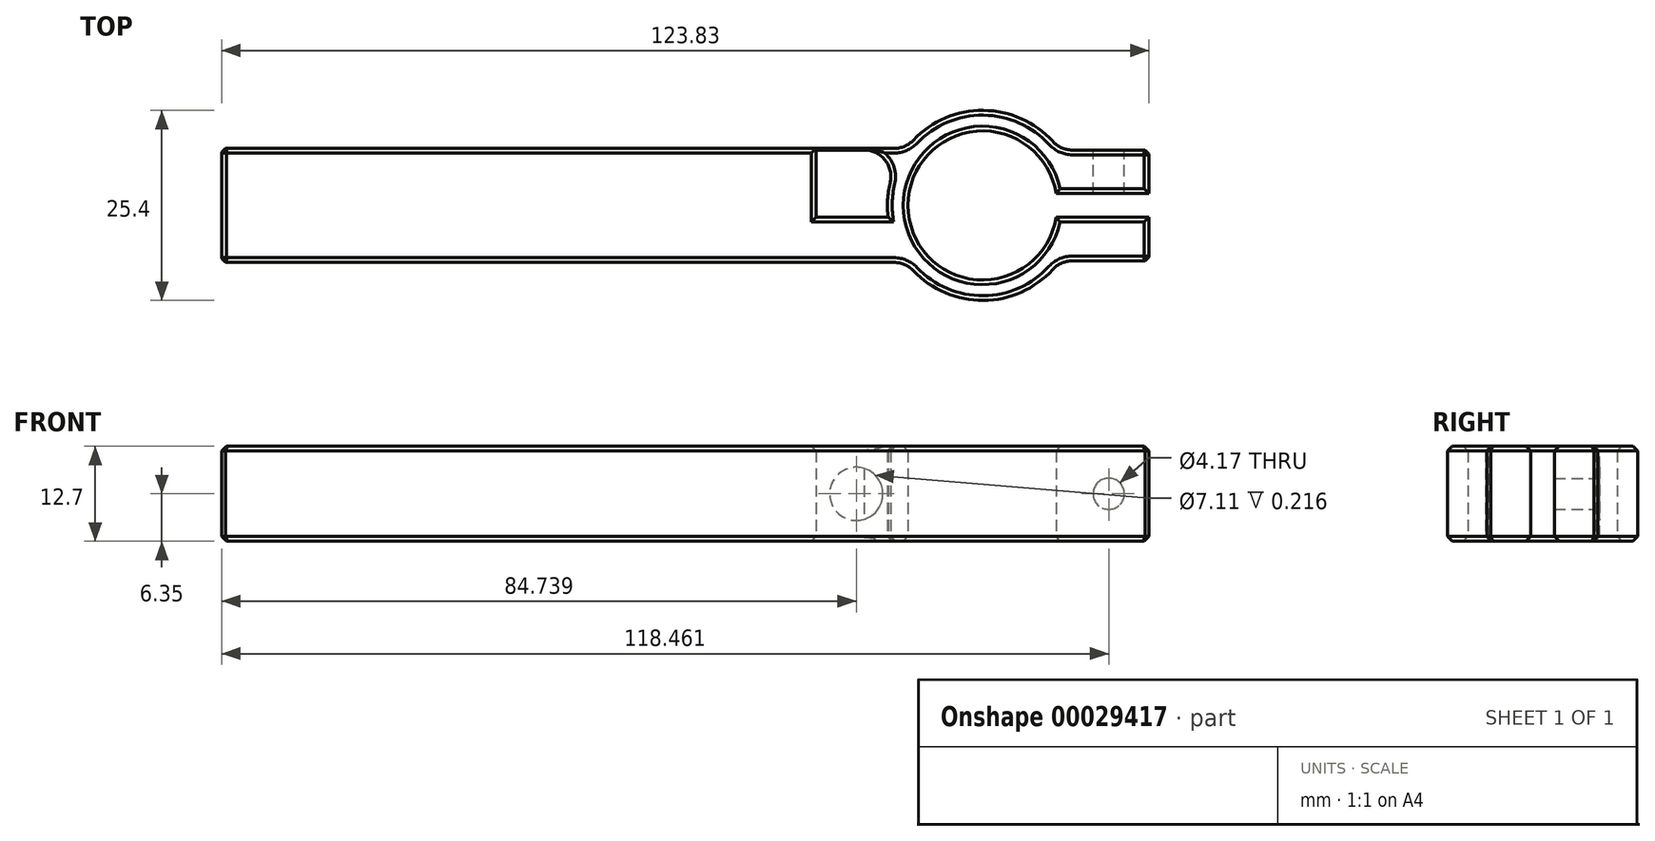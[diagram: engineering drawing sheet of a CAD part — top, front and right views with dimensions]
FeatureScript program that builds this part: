
annotation { "Feature Type Name" : "Feature", "Feature Type Description" : "" }
export const myFeature = defineFeature(function(context is Context, id is Id, definition is map)
    precondition{}
    {
        {
            var Q0;
            Q0=qCreatedBy(makeId("Top.planeOp"),FACE);
            var sketch = newSketch(context, id + "F0", { "sketchPlane" : qUnion([Q0])});
            skCircle(sketch, "E0", {"center": v(0, 0) * mm, "radius": 9.96 * mm});
            skCircle(sketch, "E1", {"center": v(0, 0) * mm, "radius": 12.7 * mm});
            skPoint(sketch, "E2.rect.middle", {"position": v(-50.8, 0) * mm});
            skLineSegment(sketch, "E3.rect.bottom", {"start": v(0, 7.62) * mm, "end": v(-101.6, 7.62) * mm});
            skLineSegment(sketch, "E3.rect.top", {"start": v(0, -7.62) * mm, "end": v(-101.6, -7.62) * mm});
            skLineSegment(sketch, "E3.rect.left", {"start": v(0, 7.62) * mm, "end": v(0, -7.62) * mm});
            skLineSegment(sketch, "E3.rect.right", {"start": v(-101.6, 7.62) * mm, "end": v(-101.6, -7.62) * mm});
            skLineSegment(sketch, "E4", {"start": v(-12.19, 0) * mm, "end": v(-50.8, 0) * mm, "construction": true});
            skLineSegment(sketch, "E5.rect.bottom", {"start": v(33.33, 1.59) * mm, "end": v(-33.33, 1.59) * mm});
            skLineSegment(sketch, "E5.rect.top", {"start": v(33.33, -1.59) * mm, "end": v(-33.33, -1.59) * mm});
            skLineSegment(sketch, "E5.rect.left", {"start": v(33.33, 1.59) * mm, "end": v(33.33, -1.59) * mm});
            skLineSegment(sketch, "E5.rect.right", {"start": v(-33.33, 1.59) * mm, "end": v(-33.33, -1.59) * mm});
            skLineSegment(sketch, "E6.rect.bottom", {"start": v(22.22, 7.4) * mm, "end": v(-22.23, 7.4) * mm});
            skLineSegment(sketch, "E6.rect.top", {"start": v(22.23, -7.4) * mm, "end": v(-22.22, -7.4) * mm});
            skLineSegment(sketch, "E6.rect.left", {"start": v(22.22, 7.4) * mm, "end": v(22.23, -7.4) * mm});
            skLineSegment(sketch, "E6.rect.right", {"start": v(-22.23, 7.4) * mm, "end": v(-22.22, -7.4) * mm});
            skSolve(sketch);
        }
        {
            var Q0;
            {var subQ3=sQuery(id+"F0.wireOp",EDGE,"E6.rect.bottom");var subQ5=sQuery(id+"F0.wireOp",EDGE,"E1");var subQ6=makeQuery(id+"F0.imprint","INTERSECT",VERTEX,{"disambiguationData":[OD(0.0)],"derivedFrom":[subQ5,subQ3]});Q0=makeQuery(id+"F0.imprint","IMPRINT",FACE,{"disambiguationData":[TD([[makeQuery(id+"F0.imprint","IMPRINT",EDGE,{"disambiguationData":[TD([[subQ6,1.0]])],"derivedFrom":subQ5}),-1.0]])]});}
            var Q1;
            {var subQ0=sQuery(id+"F0.wireOp",EDGE,"E6.rect.top");var subQ1=sQuery(id+"F0.wireOp",EDGE,"E1");var subQ2=makeQuery(id+"F0.imprint","INTERSECT",VERTEX,{"disambiguationData":[OD(0.0)],"derivedFrom":[subQ1,subQ0]});Q1=makeQuery(id+"F0.imprint","IMPRINT",FACE,{"disambiguationData":[TD([[makeQuery(id+"F0.imprint","IMPRINT",EDGE,{"disambiguationData":[TD([[subQ2,-1.0]])],"derivedFrom":subQ1}),-1.0]])]});}
            var Q2;
            {var subQ0=sQuery(id+"F0.wireOp",EDGE,"E6.rect.bottom");var subQ1=sQuery(id+"F0.wireOp",EDGE,"E0");var subQ2=makeQuery(id+"F0.imprint","INTERSECT",VERTEX,{"disambiguationData":[OD(0.0)],"derivedFrom":[subQ1,subQ0]});Q2=makeQuery(id+"F0.imprint","IMPRINT",FACE,{"disambiguationData":[TD([[makeQuery(id+"F0.imprint","IMPRINT",EDGE,{"disambiguationData":[TD([[subQ2,-1.0]])],"derivedFrom":subQ1}),-1.0]])]});}
            var Q3;
            {var subQ1=sQuery(id+"F0.wireOp",EDGE,"E0");var subQ5=sQuery(id+"F0.wireOp",EDGE,"E3.rect.top");var subQ6=makeQuery(id+"F0.imprint","INTERSECT",VERTEX,{"derivedFrom":[subQ1,subQ5]});Q3=makeQuery(id+"F0.imprint","IMPRINT",FACE,{"disambiguationData":[TD([[makeQuery(id+"F0.imprint","IMPRINT",EDGE,{"disambiguationData":[TD([[subQ6,-1.0]])],"derivedFrom":subQ1}),-1.0]])]});}
            var Q4;
            {var subQ0=sQuery(id+"F0.wireOp",EDGE,"E6.rect.bottom");var subQ1=sQuery(id+"F0.wireOp",EDGE,"E0");var subQ2=makeQuery(id+"F0.imprint","INTERSECT",VERTEX,{"disambiguationData":[OD(0.0)],"derivedFrom":[subQ1,subQ0]});Q4=makeQuery(id+"F0.imprint","IMPRINT",FACE,{"disambiguationData":[TD([[makeQuery(id+"F0.imprint","IMPRINT",EDGE,{"disambiguationData":[TD([[subQ2,1.0]])],"derivedFrom":subQ1}),-1.0]])]});}
            var Q5;
            {var subQ3=sQuery(id+"F0.wireOp",EDGE,"E0");var subQ5=sQuery(id+"F0.wireOp",EDGE,"E3.rect.bottom");var subQ6=makeQuery(id+"F0.imprint","INTERSECT",VERTEX,{"derivedFrom":[subQ3,subQ5]});Q5=makeQuery(id+"F0.imprint","IMPRINT",FACE,{"disambiguationData":[TD([[makeQuery(id+"F0.imprint","IMPRINT",EDGE,{"disambiguationData":[TD([[subQ6,-1.0]])],"derivedFrom":subQ3}),-1.0]])]});}
            var Q6;
            {var subQ0=sQuery(id+"F0.wireOp",EDGE,"E6.rect.top");var subQ1=sQuery(id+"F0.wireOp",EDGE,"E0");var subQ2=makeQuery(id+"F0.imprint","INTERSECT",VERTEX,{"disambiguationData":[OD(1.0)],"derivedFrom":[subQ1,subQ0]});Q6=makeQuery(id+"F0.imprint","IMPRINT",FACE,{"disambiguationData":[TD([[makeQuery(id+"F0.imprint","IMPRINT",EDGE,{"disambiguationData":[TD([[subQ2,-1.0]])],"derivedFrom":subQ1}),-1.0]])]});}
            var Q7;
            {var subQ3=sQuery(id+"F0.wireOp",EDGE,"E0");var subQ5=sQuery(id+"F0.wireOp",EDGE,"E5.rect.top");var subQ7=makeQuery(id+"F0.imprint","INTERSECT",VERTEX,{"disambiguationData":[OD(0.0)],"derivedFrom":[subQ3,subQ5]});Q7=makeQuery(id+"F0.imprint","IMPRINT",FACE,{"disambiguationData":[TD([[makeQuery(id+"F0.imprint","IMPRINT",EDGE,{"disambiguationData":[TD([[subQ7,-1.0]])],"derivedFrom":subQ3}),-1.0]])]});}
            var Q8;
            {var subQ1=sQuery(id+"F0.wireOp",EDGE,"E5.rect.top");var subQ5=sQuery(id+"F0.wireOp",EDGE,"E1");var subQ7=makeQuery(id+"F0.imprint","INTERSECT",VERTEX,{"disambiguationData":[OD(0.0)],"derivedFrom":[subQ5,subQ1]});Q8=makeQuery(id+"F0.imprint","IMPRINT",FACE,{"disambiguationData":[TD([[makeQuery(id+"F0.imprint","IMPRINT",EDGE,{"disambiguationData":[TD([[subQ7,-1.0]])],"derivedFrom":subQ5}),-1.0]])]});}
            var Q9;
            {var subQ3=sQuery(id+"F0.wireOp",EDGE,"E0");var subQ5=sQuery(id+"F0.wireOp",EDGE,"E6.rect.bottom");var subQ7=makeQuery(id+"F0.imprint","INTERSECT",VERTEX,{"disambiguationData":[OD(1.0)],"derivedFrom":[subQ3,subQ5]});Q9=makeQuery(id+"F0.imprint","IMPRINT",FACE,{"disambiguationData":[TD([[makeQuery(id+"F0.imprint","IMPRINT",EDGE,{"disambiguationData":[TD([[subQ7,-1.0]])],"derivedFrom":subQ3}),-1.0]])]});}
            var Q10;
            {var subQ3=sQuery(id+"F0.wireOp",EDGE,"E6.rect.bottom");var subQ5=sQuery(id+"F0.wireOp",EDGE,"E1");var subQ6=makeQuery(id+"F0.imprint","INTERSECT",VERTEX,{"disambiguationData":[OD(1.0)],"derivedFrom":[subQ5,subQ3]});Q10=makeQuery(id+"F0.imprint","IMPRINT",FACE,{"disambiguationData":[TD([[makeQuery(id+"F0.imprint","IMPRINT",EDGE,{"disambiguationData":[TD([[subQ6,-1.0]])],"derivedFrom":subQ5}),-1.0]])]});}
            var Q11;
            {var subQ13=sQuery(id+"F0.wireOp",EDGE,"E3.rect.right");Q11=makeQuery(id+"F0.imprint","IMPRINT",FACE,{"disambiguationData":[TD([[makeQuery(id+"F0.imprint","IMPRINT",EDGE,{"derivedFrom":subQ13}),1.0]])]});}
            var Q12;
            {var subQ5=sQuery(id+"F0.wireOp",EDGE,"E5.rect.right");Q12=makeQuery(id+"F0.imprint","IMPRINT",FACE,{"disambiguationData":[TD([[makeQuery(id+"F0.imprint","IMPRINT",EDGE,{"derivedFrom":subQ5}),1.0]])]});}
            var Q13;
            {var subQ3=sQuery(id+"F0.wireOp",EDGE,"E5.rect.bottom");var subQ5=sQuery(id+"F0.wireOp",EDGE,"E1");var subQ7=makeQuery(id+"F0.imprint","INTERSECT",VERTEX,{"disambiguationData":[OD(1.0)],"derivedFrom":[subQ5,subQ3]});Q13=makeQuery(id+"F0.imprint","IMPRINT",FACE,{"disambiguationData":[TD([[makeQuery(id+"F0.imprint","IMPRINT",EDGE,{"disambiguationData":[TD([[subQ7,-1.0]])],"derivedFrom":subQ5}),-1.0]])]});}
            var Q14;
            {var subQ3=sQuery(id+"F0.wireOp",EDGE,"E0");var subQ5=sQuery(id+"F0.wireOp",EDGE,"E5.rect.bottom");var subQ7=makeQuery(id+"F0.imprint","INTERSECT",VERTEX,{"disambiguationData":[OD(1.0)],"derivedFrom":[subQ3,subQ5]});Q14=makeQuery(id+"F0.imprint","IMPRINT",FACE,{"disambiguationData":[TD([[makeQuery(id+"F0.imprint","IMPRINT",EDGE,{"disambiguationData":[TD([[subQ7,-1.0]])],"derivedFrom":subQ3}),-1.0]])]});}
            var Q15;
            {var subQ0=sQuery(id+"F0.wireOp",EDGE,"E6.rect.top");var subQ3=sQuery(id+"F0.wireOp",EDGE,"E0");var subQ4=makeQuery(id+"F0.imprint","INTERSECT",VERTEX,{"disambiguationData":[OD(0.0)],"derivedFrom":[subQ3,subQ0]});Q15=makeQuery(id+"F0.imprint","IMPRINT",FACE,{"disambiguationData":[TD([[makeQuery(id+"F0.imprint","IMPRINT",EDGE,{"disambiguationData":[TD([[subQ4,-1.0]])],"derivedFrom":subQ3}),-1.0]])]});}
            extrude(context, id + "F1", {"entities" : qUnion([Q0, Q1, Q2, Q3, Q4, Q5, Q6, Q7, Q8, Q9, Q10, Q11, Q12, Q13, Q14, Q15]), "depth" : 12.7 * mm});
        }
        {
            var Q0;
            Q0=makeQuery(id+"F1.opExtrude","SWEPT_EDGE",EDGE,{"disambiguationData":[OSD([sQuery(id+"F0.wireOp",EDGE,"E1"),sQuery(id+"F0.wireOp",EDGE,"E3.rect.bottom")])]});
            var Q1;
            Q1=makeQuery(id+"F1.opExtrude","SWEPT_EDGE",EDGE,{"disambiguationData":[OSD([sQuery(id+"F0.wireOp",EDGE,"E1"),sQuery(id+"F0.wireOp",EDGE,"E3.rect.top")])]});
            var Q2;
            Q2=makeQuery(id+"F1.opExtrude","SWEPT_EDGE",EDGE,{"disambiguationData":[OSD([sQuery(id+"F0.wireOp",EDGE,"E1"),sQuery(id+"F0.wireOp",EDGE,"E6.rect.top")])]});
            var Q3;
            Q3=makeQuery(id+"F1.opExtrude","SWEPT_EDGE",EDGE,{"disambiguationData":[OSD([sQuery(id+"F0.wireOp",EDGE,"E1"),sQuery(id+"F0.wireOp",EDGE,"E6.rect.bottom")])]});
            fillet(context, id + "F2", {"entities" : qUnion([Q0, Q1, Q2, Q3]), "radius" : 3.56 * mm, "tangentPropagation" : true, "allowEdgeOverflow" : false});
        }
        {
            var Q0;
            Q0=makeQuery(id+"F1.opExtrude","SWEPT_EDGE",EDGE,{"disambiguationData":[OSD([sQuery(id+"F0.wireOp",EDGE,"E3.rect.bottom"),sQuery(id+"F0.wireOp",EDGE,"E3.rect.right")])]});
            var Q1;
            Q1=makeQuery(id+"F1.opExtrude","SWEPT_EDGE",EDGE,{"disambiguationData":[OSD([sQuery(id+"F0.wireOp",EDGE,"E3.rect.top"),sQuery(id+"F0.wireOp",EDGE,"E3.rect.right")])]});
            var Q2;
            Q2=makeQuery(id+"F1.opExtrude","SWEPT_EDGE",EDGE,{"disambiguationData":[OSD([sQuery(id+"F0.wireOp",EDGE,"E6.rect.bottom"),sQuery(id+"F0.wireOp",EDGE,"E6.rect.left")])]});
            var Q3;
            Q3=makeQuery(id+"F1.opExtrude","SWEPT_EDGE",EDGE,{"disambiguationData":[OSD([sQuery(id+"F0.wireOp",EDGE,"E6.rect.top"),sQuery(id+"F0.wireOp",EDGE,"E6.rect.left")])]});
            chamfer(context, id + "F3", {"entities" : qUnion([Q0, Q1, Q2, Q3]), "width" : 0.5 * mm, "tangentPropagation" : true});
        }
        {
            var Q0;
            Q0=makeQuery(id+"F1.opExtrude","SWEPT_FACE",FACE,{"disambiguationData":[OSD([sQuery(id+"F0.wireOp",EDGE,"E6.rect.bottom")])]});
            var sketch = newSketch(context, id + "F4", { "sketchPlane" : qUnion([Q0])});
            skLineSegment(sketch, "E7", {"start": v(-12, 6.35) * mm, "end": v(-21.72, 6.35) * mm, "construction": true});
            skCircle(sketch, "E8", {"center": v(-16.86, 6.35) * mm, "radius": 1.73 * mm});
            skSolve(sketch);
        }
        {
            var Q0;
            Q0 = qSketchRegion(id + "F4", true);
            extrude(context, id + "F5", {"entities" : qUnion([Q0]), "operationType" : NewBodyOperationType.REMOVE, "endBound" : BoundingType.THROUGH_ALL, "oppositeDirection" : true, "depth" : 25.4 * mm});
        }
        {
            var Q0;
            Q0=makeQuery(id+"F1.opExtrude","SWEPT_FACE",FACE,{"disambiguationData":[OSD([sQuery(id+"F0.wireOp",EDGE,"E6.rect.bottom")])]});
            var sketch = newSketch(context, id + "F6", { "sketchPlane" : qUnion([Q0])});
            skCircle(sketch, "E9", {"center": v(-16.86, 6.35) * mm, "radius": 2.08 * mm});
            skSolve(sketch);
        }
        {
            var Q0;
            Q0 = qSketchRegion(id + "F6", true);
            var Q1;
            Q1=makeQuery(id+"F1.opExtrude","SWEPT_FACE",FACE,{"disambiguationData":[OSD([sQuery(id+"F0.wireOp",EDGE,"E5.rect.bottom")])]});
            extrude(context, id + "F7", {"entities" : qUnion([Q0]), "operationType" : NewBodyOperationType.REMOVE, "endBound" : BoundingType.UP_TO_SURFACE, "oppositeDirection" : true, "endBoundEntityFace" : qUnion([Q1]), "depth" : 25.4 * mm});
        }
        {
            var Q0;
            Q0=makeQuery(id+"F1.opExtrude","SWEPT_FACE",FACE,{"disambiguationData":[OSD([sQuery(id+"F0.wireOp",EDGE,"E6.rect.bottom")])]});
            var sketch = newSketch(context, id + "F8", { "sketchPlane" : qUnion([Q0])});
            skCircle(sketch, "E10", {"center": v(-16.86, 6.35) * mm, "radius": 3.56 * mm});
            skSolve(sketch);
        }
        {
            var Q0;
            Q0 = qSketchRegion(id + "F8", true);
            extrude(context, id + "F9", {"entities" : qUnion([Q0]), "operationType" : NewBodyOperationType.REMOVE, "oppositeDirection" : true, "depth" : 4.2 * mm});
        }
        {
            var Q0;
            Q0=makeQuery(id+"F1.opExtrude","CAP_FACE",FACE,{"disambiguationData":[OSD([sQuery(id+"F0.wireOp",EDGE,"E0"),sQuery(id+"F0.wireOp",EDGE,"E1"),sQuery(id+"F0.wireOp",EDGE,"E3.rect.bottom"),sQuery(id+"F0.wireOp",EDGE,"E3.rect.top"),sQuery(id+"F0.wireOp",EDGE,"E3.rect.right"),sQuery(id+"F0.wireOp",EDGE,"E5.rect.bottom"),sQuery(id+"F0.wireOp",EDGE,"E5.rect.top"),sQuery(id+"F0.wireOp",EDGE,"E6.rect.bottom"),sQuery(id+"F0.wireOp",EDGE,"E6.rect.top"),sQuery(id+"F0.wireOp",EDGE,"E6.rect.left")])],"isStart":false});
            var Q1;
            Q1=makeQuery(id+"F1.opExtrude","CAP_FACE",FACE,{"disambiguationData":[OSD([sQuery(id+"F0.wireOp",EDGE,"E0"),sQuery(id+"F0.wireOp",EDGE,"E1"),sQuery(id+"F0.wireOp",EDGE,"E3.rect.bottom"),sQuery(id+"F0.wireOp",EDGE,"E3.rect.top"),sQuery(id+"F0.wireOp",EDGE,"E3.rect.right"),sQuery(id+"F0.wireOp",EDGE,"E5.rect.bottom"),sQuery(id+"F0.wireOp",EDGE,"E5.rect.top"),sQuery(id+"F0.wireOp",EDGE,"E6.rect.bottom"),sQuery(id+"F0.wireOp",EDGE,"E6.rect.top"),sQuery(id+"F0.wireOp",EDGE,"E6.rect.left")])],"isStart":true});
            chamfer(context, id + "F10", {"entities" : qUnion([Q0, Q1]), "width" : 0.64 * mm, "tangentPropagation" : true});
        }
    });
